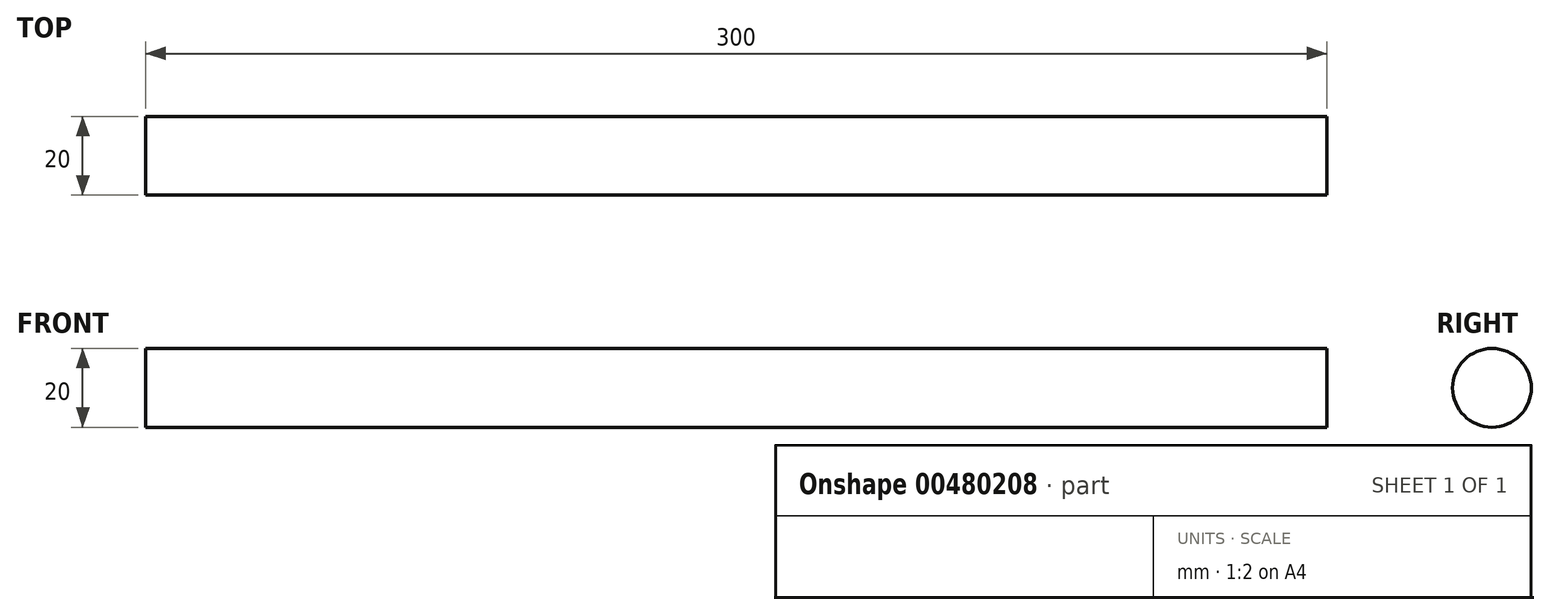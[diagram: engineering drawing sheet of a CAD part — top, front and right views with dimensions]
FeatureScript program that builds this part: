
annotation { "Feature Type Name" : "Feature", "Feature Type Description" : "" }
export const myFeature = defineFeature(function(context is Context, id is Id, definition is map)
    precondition{}
    {
        {
            var Q0;
            Q0=qCreatedBy(makeId("Right.planeOp"),FACE);
            var sketch = newSketch(context, id + "F0", { "sketchPlane" : qUnion([Q0])});
            skCircle(sketch, "E0", {"center": v(0, -1.1) * mm, "radius": 10 * mm});
            skSolve(sketch);
        }
        {
            var Q0;
            Q0 = qSketchRegion(id + "F0", true);
            extrude(context, id + "F1", {"entities" : qUnion([Q0]), "depth" : 300 * mm});
        }
    });
